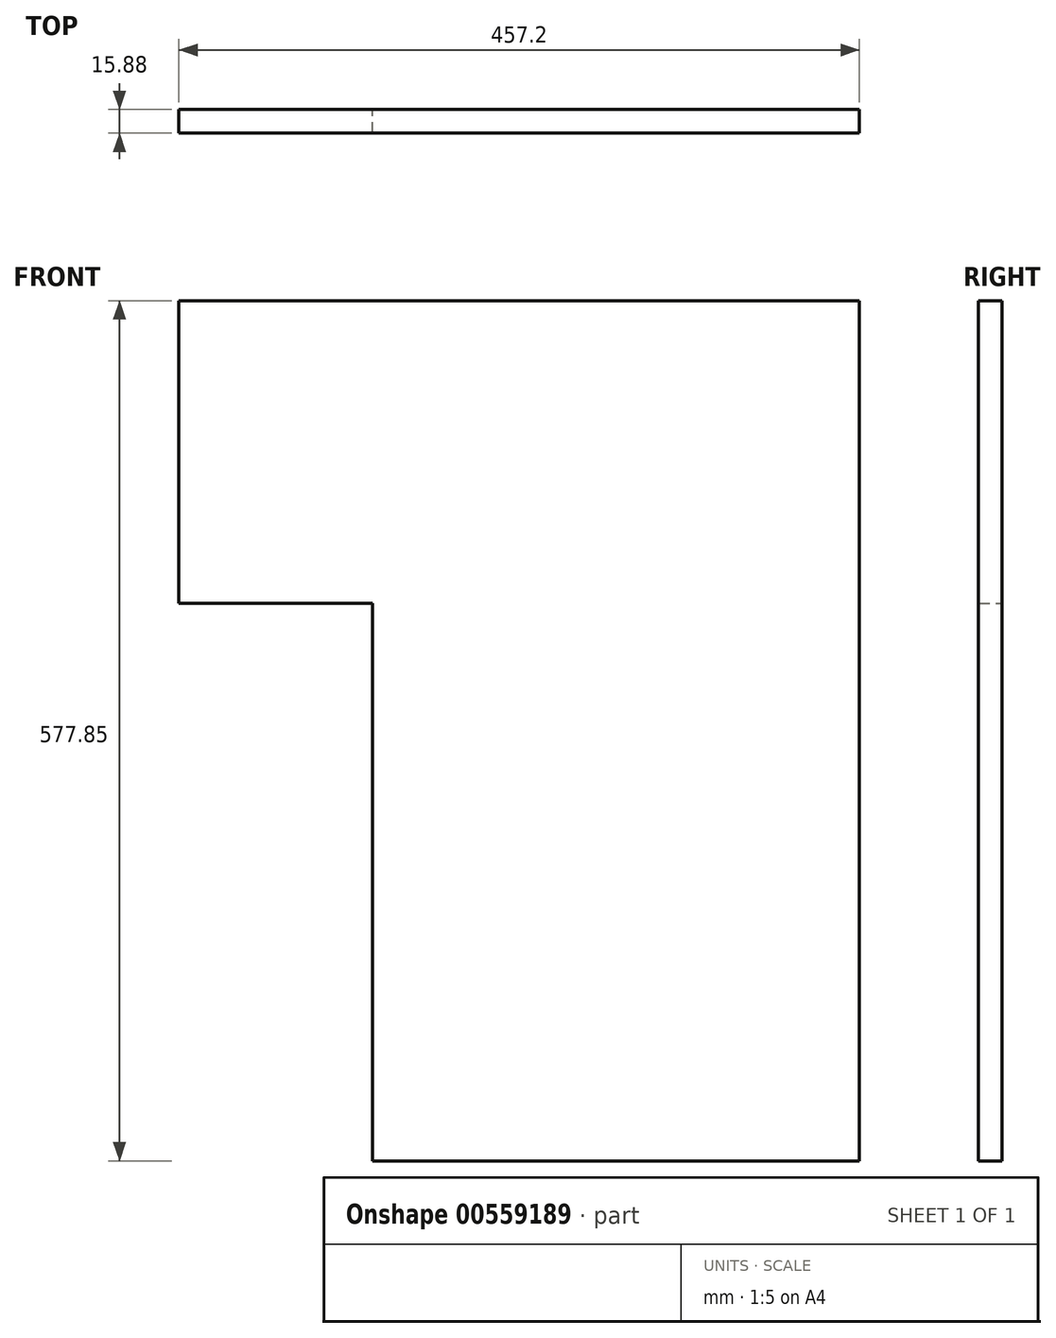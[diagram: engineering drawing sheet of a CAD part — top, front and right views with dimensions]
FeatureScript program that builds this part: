
annotation { "Feature Type Name" : "Feature", "Feature Type Description" : "" }
export const myFeature = defineFeature(function(context is Context, id is Id, definition is map)
    precondition{}
    {
        {
            var Q0;
            Q0=qCreatedBy(makeId("Front.planeOp"),FACE);
            var sketch = newSketch(context, id + "F0", { "sketchPlane" : qUnion([Q0])});
            skLineSegment(sketch, "E0", {"start": v(-68.23, 114.44) * mm, "end": v(388.97, 114.44) * mm});
            skLineSegment(sketch, "E1", {"start": v(388.97, 114.44) * mm, "end": v(388.97, -463.4) * mm});
            skLineSegment(sketch, "E2", {"start": v(388.97, -463.4) * mm, "end": v(61.94, -463.4) * mm});
            skLineSegment(sketch, "E3", {"start": v(61.94, -463.4) * mm, "end": v(61.94, -88.76) * mm});
            skLineSegment(sketch, "E4", {"start": v(-68.23, 114.44) * mm, "end": v(-68.23, -88.76) * mm});
            skLineSegment(sketch, "E5", {"start": v(-68.23, -88.76) * mm, "end": v(61.94, -88.76) * mm});
            skSolve(sketch);
        }
        {
            var Q0;
            Q0 = qSketchRegion(id + "F0", true);
            extrude(context, id + "F1", {"entities" : qUnion([Q0]), "depth" : 15.88 * mm, "offsetDistance" : 25.4 * mm});
        }
    });
